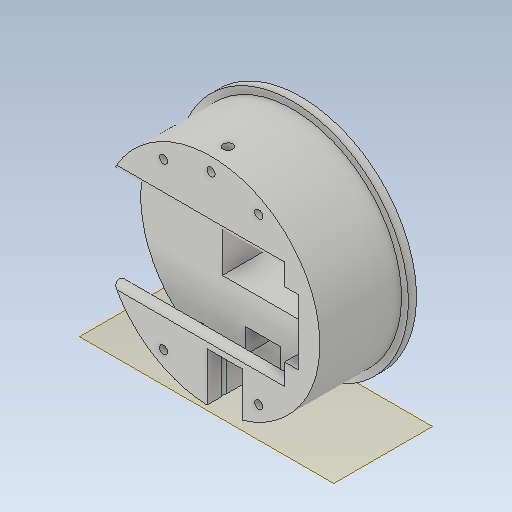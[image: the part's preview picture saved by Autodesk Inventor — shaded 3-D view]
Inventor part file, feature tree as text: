
AUTODESK INVENTOR PART (.ipt)
format: ipt  version: 2020.1 (Build 241239000, 239)  size: 377,856 bytes
history: native  units: mm
features: extrude x11, sketch x11, fillet x2, mirror x1, plane x1
ambient origin geometry x8: Origin, YZ Plane, XZ Plane, XY Plane, X Axis, Y Axis, Z Axis, Center Point
bodies: Solid1 (feature_tree)
feature tree (26):
  extrude  "base"  Depth=30.0mm TaperAngle=0.0deg
  extrude  "horse_tail_1"  Depth=30.0mm
  mirror  "horse_tail_2"
  fillet  "fillet_horse_tail"  Radius=15.0mm
  extrude  "lock_arm"  Depth=20.0mm
  extrude  "servo_place"  Depth=20.0mm
  extrude  "base_hold"  Depth=3.5mm
  extrude  "horse_tal_end"  Depth=30.0mm
  extrude  "reinforcement_holes"  Depth=10.0mm
  extrude  "cable_hole"  Depth=40.0mm
  extrude  "Extrusion10"  Depth=30.0mm
  fillet  "Fillet3"  Radius=85.0mm
  plane  "Work Plane1"
  extrude  "Extrusion11"  Depth=8.0mm
  extrude  "Extrusion12"  Depth=10.0mm
  sketch  "Sketch1"  dims[d0=80.0mm d1=30.0mm d2=0.0mm]
  sketch  "Sketch3"  dims[d10=30.0mm d11=0.0mm d12=2.0mm d13=15.0mm]
  sketch  "Sketch4"  dims[d14=15.0mm d15=20.0mm]
  sketch  "Sketch5"  dims[d16=135.0deg d17=20.0mm]
  sketch  "Sketch6"  dims[d18=135.0deg d20=3.5mm]
  sketch  "Sketch7"  dims[d21=30.0mm d22=0.0mm d23=8.0mm]
  sketch  "Sketch8"  dims[d24=10.0mm d25=10.0mm]
  sketch  "Sketch9"  dims[d26=20.0mm d27=40.0mm]
  sketch  "Sketch10"  dims[d28=30.0mm d29=0.0mm d30=20.0mm d31=85.0mm]
  sketch  "Sketch11"  dims[d32=3.0mm d33=0.0mm d34=8.0mm]
  sketch  "Sketch12"  dims[d35=12.0mm d36=12.0mm d37=5.0mm d38=5.0mm d39=10.0mm d40=0.0mm d41=70.0mm d42=60.0deg d43=120.0deg d44=3.0mm d45=3.0mm d46=3.0mm d47=3.0mm d48=3.0mm d49=3.0mm d50=10.0mm d51=0.0mm d60=10.0mm d61=0.0mm d62=22.0mm d63=5.0mm d64=6.5mm d65=9.0mm d66=13.0mm d67=9.0mm d68=90.0deg d69=270.0deg d74=40.0mm d75=7.5mm d76=0.0mm d77=5.0mm d78=0.0mm d79=5.0mm d80=45.0deg d81=2.0mm d82=180.0deg d83=6.0mm d84=90.0deg d85=2.0mm d86=2.0mm d87=0.0mm d88=13.0mm d89=20.0mm d90=10.0mm d91=0.0mm]
